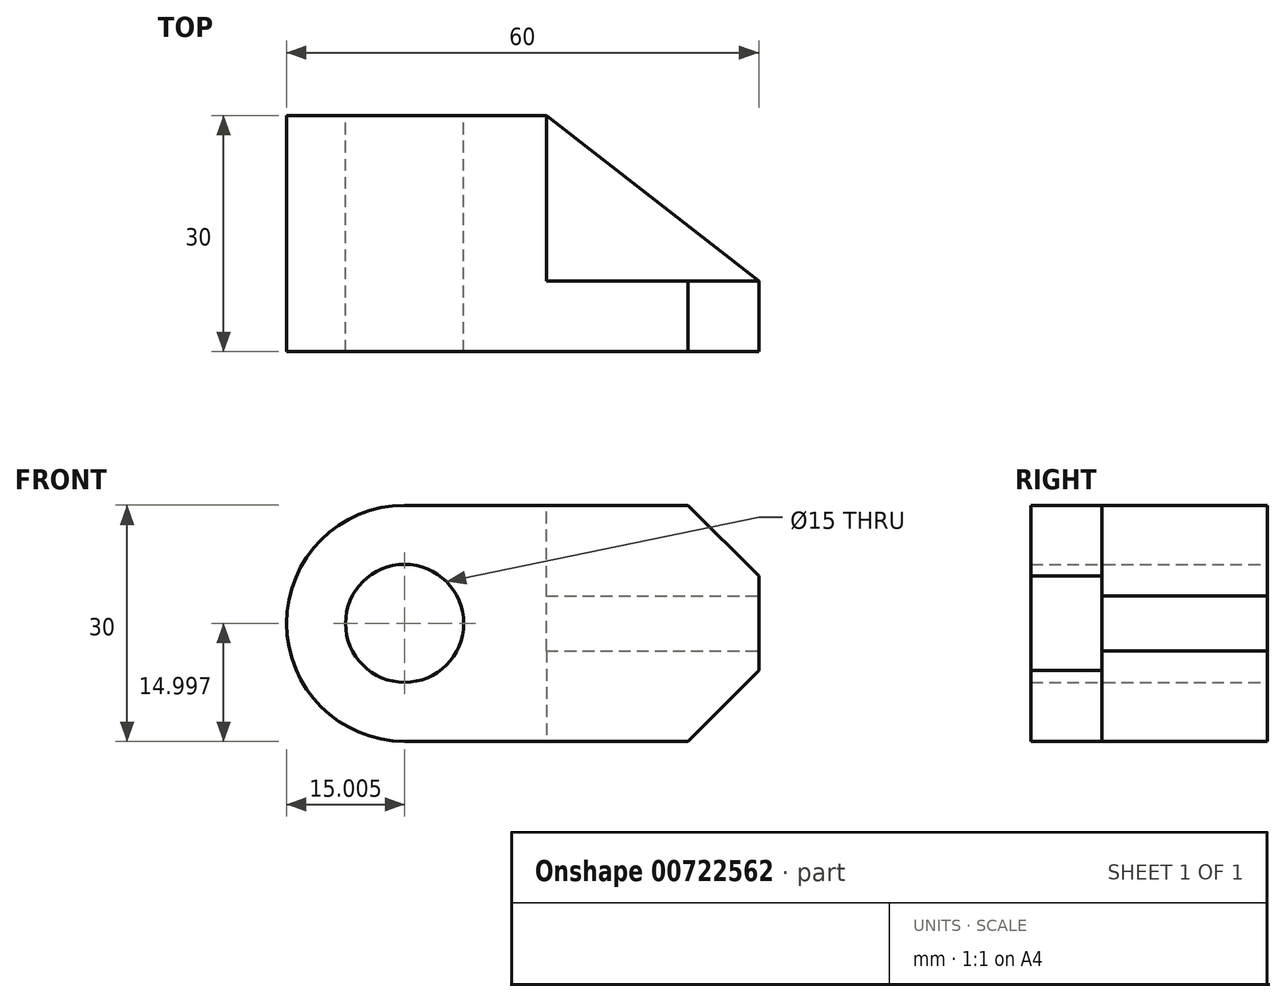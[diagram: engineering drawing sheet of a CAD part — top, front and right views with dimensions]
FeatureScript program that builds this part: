
annotation { "Feature Type Name" : "Feature", "Feature Type Description" : "" }
export const myFeature = defineFeature(function(context is Context, id is Id, definition is map)
    precondition{}
    {
        {
            var Q0;
            Q0=qCreatedBy(makeId("Front.planeOp"),FACE);
            var sketch = newSketch(context, id + "F0", { "sketchPlane" : qUnion([Q0])});
            skLineSegment(sketch, "E0.bottom", {"start": v(-31.16, 21.33) * mm, "end": v(28.84, 21.33) * mm});
            skLineSegment(sketch, "E0.top", {"start": v(-31.16, -8.67) * mm, "end": v(28.84, -8.67) * mm});
            skLineSegment(sketch, "E0.left", {"start": v(-31.16, 21.33) * mm, "end": v(-31.16, -8.67) * mm});
            skLineSegment(sketch, "E0.right", {"start": v(28.84, 21.33) * mm, "end": v(28.84, -8.67) * mm});
            skSolve(sketch);
        }
        {
            var Q0;
            Q0=makeQuery(id+"F0.imprint","IMPRINT",FACE,{"disambiguationData":[TD([[makeQuery(id+"F0.imprint","IMPRINT",EDGE,{"derivedFrom":sQuery(id+"F0.wireOp",EDGE,"E0.bottom")}),-1.0]])]});
            extrude(context, id + "F1", {"entities" : qUnion([Q0]), "depth" : 30 * mm, "offsetDistance" : 25.4 * mm});
        }
        {
            var Q0;
            Q0=makeQuery(id+"F1.opExtrude","SWEPT_EDGE",EDGE,{"disambiguationData":[OSD([sQuery(id+"F0.wireOp",EDGE,"E0.bottom"),sQuery(id+"F0.wireOp",EDGE,"E0.left")])]});
            var Q1;
            Q1=makeQuery(id+"F1.opExtrude","SWEPT_EDGE",EDGE,{"disambiguationData":[OSD([sQuery(id+"F0.wireOp",EDGE,"E0.top"),sQuery(id+"F0.wireOp",EDGE,"E0.left")])]});
            fillet(context, id + "F2", {"entities" : qUnion([Q0, Q1]), "radius" : 15 * mm, "tangentPropagation" : true, "allowEdgeOverflow" : false});
        }
        {
            var Q0;
            Q0=makeQuery(id+"F1.opExtrude","SWEPT_FACE",FACE,{"disambiguationData":[OSD([sQuery(id+"F0.wireOp",EDGE,"E0.bottom")])]});
            var sketch = newSketch(context, id + "F3", { "sketchPlane" : qUnion([Q0])});
            skLineSegment(sketch, "E1", {"start": v(-16.16, 0) * mm, "end": v(1.84, 0) * mm});
            skLineSegment(sketch, "E2", {"start": v(1.84, 0) * mm, "end": v(1.84, -21) * mm});
            skLineSegment(sketch, "E3", {"start": v(12.18, -30) * mm, "end": v(12.18, -25.01) * mm, "construction": true});
            skLineSegment(sketch, "E4", {"start": v(1.84, -21) * mm, "end": v(28.84, -21) * mm});
            skLineSegment(sketch, "E5", {"start": v(1.84, 0) * mm, "end": v(28.84, -21) * mm});
            skLineSegment(sketch, "E6", {"start": v(1.84, 0) * mm, "end": v(28.84, 0) * mm});
            skLineSegment(sketch, "E7", {"start": v(28.84, 0) * mm, "end": v(28.84, -21) * mm});
            skSolve(sketch);
        }
        {
            var Q0;
            Q0=makeQuery(id+"F3.imprint","IMPRINT",FACE,{"disambiguationData":[TD([[makeQuery(id+"F3.imprint","IMPRINT",EDGE,{"derivedFrom":sQuery(id+"F3.wireOp",EDGE,"E5")}),1.0]])]});
            extrude(context, id + "F4", {"entities" : qUnion([Q0]), "operationType" : NewBodyOperationType.REMOVE, "oppositeDirection" : true, "depth" : 45.97 * mm, "offsetDistance" : 25.4 * mm});
        }
        {
            var Q0;
            Q0=makeQuery(id+"F3.imprint","IMPRINT",FACE,{"disambiguationData":[TD([[makeQuery(id+"F3.imprint","IMPRINT",EDGE,{"derivedFrom":sQuery(id+"F3.wireOp",EDGE,"E2")}),1.0]])]});
            extrude(context, id + "F5", {"entities" : qUnion([Q0]), "operationType" : NewBodyOperationType.REMOVE, "oppositeDirection" : true, "depth" : 11.5 * mm, "offsetDistance" : 25.4 * mm});
        }
        {
            var Q0;
            Q0=makeQuery(id+"F1.opExtrude","SWEPT_FACE",FACE,{"disambiguationData":[OSD([sQuery(id+"F0.wireOp",EDGE,"E0.top")])]});
            var sketch = newSketch(context, id + "F6", { "sketchPlane" : qUnion([Q0])});
            skLineSegment(sketch, "E8", {"start": v(1.84, 0) * mm, "end": v(1.84, 21) * mm});
            skLineSegment(sketch, "E9", {"start": v(1.84, 21) * mm, "end": v(28.84, 21) * mm});
            skLineSegment(sketch, "E10", {"start": v(28.84, 21) * mm, "end": v(1.84, 0) * mm});
            skSolve(sketch);
        }
        {
            var Q0;
            Q0 = qSketchRegion(id + "F6", true);
            extrude(context, id + "F7", {"entities" : qUnion([Q0]), "operationType" : NewBodyOperationType.REMOVE, "oppositeDirection" : true, "depth" : 11.5 * mm, "offsetDistance" : 25.4 * mm});
        }
        {
            var Q0;
            Q0=makeQuery(id+"F1.opExtrude","CAP_FACE",FACE,{"disambiguationData":[OSD([sQuery(id+"F0.wireOp",EDGE,"E0.bottom"),sQuery(id+"F0.wireOp",EDGE,"E0.top"),sQuery(id+"F0.wireOp",EDGE,"E0.left"),sQuery(id+"F0.wireOp",EDGE,"E0.right")])],"isStart":true});
            var sketch = newSketch(context, id + "F8", { "sketchPlane" : qUnion([Q0])});
            skCircle(sketch, "E11", {"center": v(16.16, 6.33) * mm, "radius": 7.5 * mm});
            skSolve(sketch);
        }
        {
            var Q0;
            Q0=makeQuery(id+"F8.imprint","IMPRINT",FACE,{"disambiguationData":[TD([[makeQuery(id+"F8.imprint","IMPRINT",EDGE,{"derivedFrom":sQuery(id+"F8.wireOp",EDGE,"E11")}),1.0]])]});
            extrude(context, id + "F9", {"entities" : qUnion([Q0]), "operationType" : NewBodyOperationType.REMOVE, "oppositeDirection" : true, "depth" : 31 * mm, "offsetDistance" : 25.4 * mm});
        }
        {
            var Q0;
            Q0=makeQuery(id+"F7.boolean.opBoolean","COPY",FACE,{"derivedFrom":makeQuery(id+"F7.opExtrude","SWEPT_FACE",FACE,{"disambiguationData":[OSD([sQuery(id+"F6.wireOp",EDGE,"E9")])]})});
            var sketch = newSketch(context, id + "F10", { "sketchPlane" : qUnion([Q0])});
            skLineSegment(sketch, "E12", {"start": v(-28.84, -8.67) * mm, "end": v(-19.84, -8.67) * mm});
            skPoint(sketch, "E13.end.orphan", {"position": v(-28.84, 0) * mm});
            skLineSegment(sketch, "E14", {"start": v(-28.84, -8.67) * mm, "end": v(-28.84, 0.32) * mm});
            skLineSegment(sketch, "E15", {"start": v(-28.84, 0.32) * mm, "end": v(-19.84, -8.67) * mm});
            skSolve(sketch);
        }
        {
            var Q0;
            Q0=makeQuery(id+"F10.imprint","IMPRINT",FACE,{"disambiguationData":[TD([[makeQuery(id+"F10.imprint","IMPRINT",EDGE,{"derivedFrom":sQuery(id+"F10.wireOp",EDGE,"E12")}),-1.0]])]});
            extrude(context, id + "F11", {"entities" : qUnion([Q0]), "operationType" : NewBodyOperationType.REMOVE, "oppositeDirection" : true, "depth" : 25.4 * mm, "offsetDistance" : 25.4 * mm});
        }
        {
            var Q0;
            Q0=makeQuery(id+"F5.boolean.opBoolean","COPY",FACE,{"derivedFrom":makeQuery(id+"F5.opExtrude","SWEPT_FACE",FACE,{"disambiguationData":[OSD([sQuery(id+"F3.wireOp",EDGE,"E4")])]})});
            var sketch = newSketch(context, id + "F12", { "sketchPlane" : qUnion([Q0])});
            skLineSegment(sketch, "E16", {"start": v(-28.84, 21.33) * mm, "end": v(-28.84, 12.33) * mm});
            skLineSegment(sketch, "E17", {"start": v(-28.84, 21.33) * mm, "end": v(-19.85, 21.33) * mm});
            skLineSegment(sketch, "E18", {"start": v(-19.85, 21.33) * mm, "end": v(-28.84, 12.33) * mm});
            skSolve(sketch);
        }
        {
            var Q0;
            Q0=makeQuery(id+"F12.imprint","IMPRINT",FACE,{"disambiguationData":[TD([[makeQuery(id+"F12.imprint","IMPRINT",EDGE,{"derivedFrom":sQuery(id+"F12.wireOp",EDGE,"E16")}),-1.0]])]});
            extrude(context, id + "F13", {"entities" : qUnion([Q0]), "operationType" : NewBodyOperationType.REMOVE, "oppositeDirection" : true, "depth" : 25.4 * mm, "offsetDistance" : 25.4 * mm});
        }
    });
